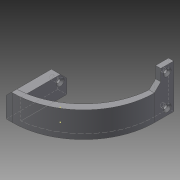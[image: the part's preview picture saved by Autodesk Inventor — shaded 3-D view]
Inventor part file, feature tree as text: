
AUTODESK INVENTOR PART (.ipt)
format: ipt  version: 2015 (Build 190159000, 159)  size: 199,168 bytes
history: native  units: mm
features: sketch x13, extrude x9, hole x2, chamfer x2, fillet x1
ambient origin geometry x8: Origin, YZ Plane, XZ Plane, XY Plane, X Axis, Y Axis, Z Axis, Center Point
bodies: Solid1 (feature_tree)
feature tree (27):
  extrude  "Extrusion1"  Depth=40.0mm
  hole  "Hole1"  [1 undecoded]
  extrude  "Extrusion2"  Depth=60.0mm
  extrude  "Extrusion3"  Depth=4.0mm
  extrude  "Extrusion8"  Depth=10.0mm TaperAngle=0.0deg
  extrude  "Extrusion9"  Depth=23.0mm
  sketch  "Sketch12"  dims[d21=5.0mm d22=23.0mm]
  extrude  "Extrusion10"  Depth=5.0mm
  sketch  "Sketch14"  dims[d25=4.0mm d26=0.0mm d40=10.0mm d41=0.0mm]
  extrude  "Extrusion11"  Depth=10.0mm TaperAngle=0.0deg
  extrude  "Extrusion12"  Depth=60.0mm
  extrude  "Extrusion13"  Depth=4.0mm
  hole  "Hole3"  [1 undecoded]
  fillet  "Fillet4"  Radius=4.0mm
  chamfer  "Chamfer2"  Distance=20.0mm
  chamfer  "Chamfer3"  Distance=6.0mm
  sketch  "Sketch1"  dims[d0=7.0mm d1=40.0mm]
  sketch  "Sketch2"  dims[d2=10.0mm d3=0.0mm d4=5.0mm]
  sketch  "Sketch3"  dims[d5=5.0mm]
  sketch  "Sketch4"  dims[d6=3.0mm d7=6.0mm d8=6.0mm d9=2.0mm d10=90.0deg d11=8.0mm d12=20.594885mm d13=60.0mm]
  sketch  "Sketch9"  dims[d14=4.0mm d15=4.0mm]
  sketch  "Sketch10"  dims[d16=65.0mm d17=10.0mm d18=0.0mm]
  sketch  "Sketch13"  dims[d23=11.0mm d24=5.0mm]
  sketch  "Sketch15"  dims[d42=10.0mm d43=0.0mm d53=60.0mm]
  sketch  "Sketch16"  dims[d54=4.0mm d55=4.0mm]
  sketch  "Sketch17"  dims[d56=6.0mm d57=0.0mm d58=20.0mm d59=0.0mm d60=4.0mm]
  sketch  "Sketch18"  dims[d61=4.0mm d62=20.0mm d63=0.0mm d64=6.0mm d65=0.0mm d66=5.0mm d67=5.0mm d68=3.0mm d69=6.0mm d70=6.0mm d71=2.0mm d72=90.0deg d73=8.0mm d74=20.594885mm d75=55.0mm d76=4.0mm d77=2.0mm d78=45.0deg d79=5.0mm d80=2.0mm d81=45.0deg]
note: 2 required parameter values undecoded (feature->parameter linkage not recoverable at this tier; creation-order binding heuristic only, values carry confidence <= 0.55)
